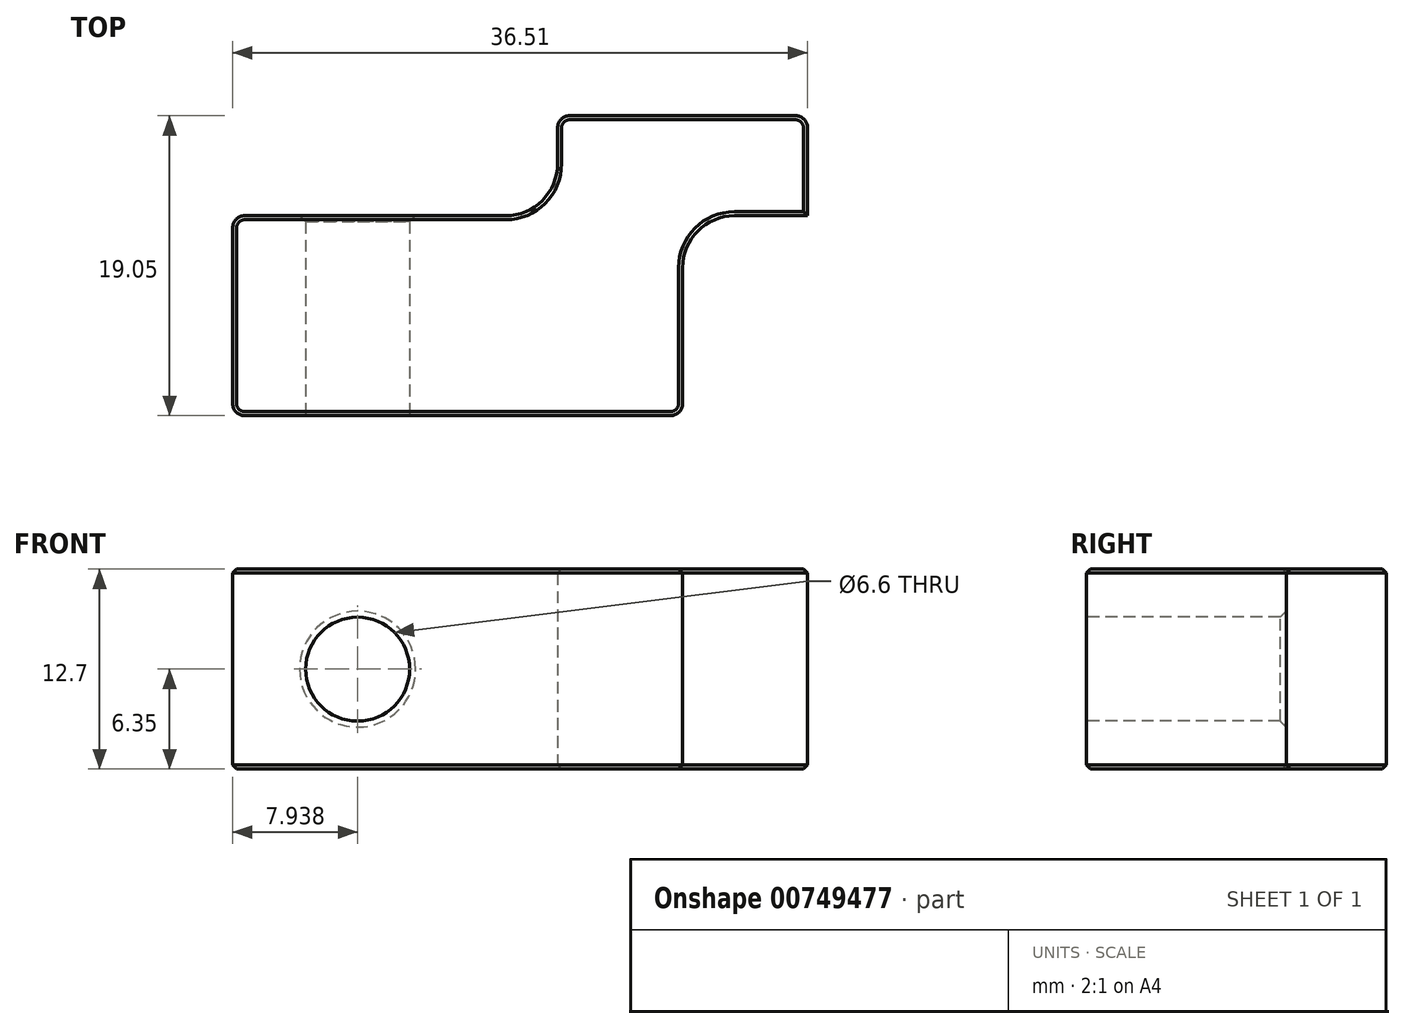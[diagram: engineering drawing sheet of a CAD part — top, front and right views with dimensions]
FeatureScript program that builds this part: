
annotation { "Feature Type Name" : "Feature", "Feature Type Description" : "" }
export const myFeature = defineFeature(function(context is Context, id is Id, definition is map)
    precondition{}
    {
        {
            var Q0;
            Q0=qCreatedBy(makeId("Top.planeOp"),FACE);
            var sketch = newSketch(context, id + "F0", { "sketchPlane" : qUnion([Q0])});
            skLineSegment(sketch, "E0", {"start": v(0, 0) * mm, "end": v(28.58, 0) * mm});
            skLineSegment(sketch, "E1", {"start": v(28.58, 0) * mm, "end": v(28.58, 9.4) * mm});
            skLineSegment(sketch, "E2", {"start": v(31.88, 12.7) * mm, "end": v(36.51, 12.7) * mm});
            skLineSegment(sketch, "E3", {"start": v(36.51, 12.7) * mm, "end": v(36.51, 19.05) * mm});
            skLineSegment(sketch, "E4", {"start": v(36.51, 19.05) * mm, "end": v(20.64, 19.05) * mm});
            skLineSegment(sketch, "E5", {"start": v(20.64, 19.05) * mm, "end": v(20.64, 16) * mm});
            skLineSegment(sketch, "E6", {"start": v(17.34, 12.7) * mm, "end": v(0, 12.7) * mm});
            skLineSegment(sketch, "E7", {"start": v(0, 12.7) * mm, "end": v(0, 0) * mm});
            skPoint(sketch, "E8.visualSharp", {"position": v(20.64, 12.7) * mm});
            skArc(sketch, "E8.filletArc", {"start": v(17.34, 12.7) * mm, "mid": v(19.67, 13.67) * mm, "end": v(20.64, 16) * mm});
            skPoint(sketch, "E9.visualSharp", {"position": v(28.58, 12.7) * mm});
            skArc(sketch, "E9.filletArc", {"start": v(31.88, 12.7) * mm, "mid": v(29.54, 11.73) * mm, "end": v(28.58, 9.4) * mm});
            skSolve(sketch);
        }
        {
            var Q0;
            Q0 = qSketchRegion(id + "F0", true);
            extrude(context, id + "F1", {"entities" : qUnion([Q0]), "depth" : 12.7 * mm, "offsetDistance" : 25.4 * mm});
        }
        {
            var Q0;
            Q0=makeQuery(id+"F1.opExtrude","SWEPT_EDGE",EDGE,{"disambiguationData":[OSD([sQuery(id+"F0.wireOp",EDGE,"E0"),sQuery(id+"F0.wireOp",EDGE,"E1")])]});
            var Q1;
            Q1=makeQuery(id+"F1.opExtrude","SWEPT_EDGE",EDGE,{"disambiguationData":[OSD([sQuery(id+"F0.wireOp",EDGE,"E0"),sQuery(id+"F0.wireOp",EDGE,"E7")])]});
            var Q2;
            Q2=makeQuery(id+"F1.opExtrude","SWEPT_EDGE",EDGE,{"disambiguationData":[OSD([sQuery(id+"F0.wireOp",EDGE,"E6"),sQuery(id+"F0.wireOp",EDGE,"E7")])]});
            var Q3;
            Q3=makeQuery(id+"F1.opExtrude","SWEPT_EDGE",EDGE,{"disambiguationData":[OSD([sQuery(id+"F0.wireOp",EDGE,"E4"),sQuery(id+"F0.wireOp",EDGE,"E5")])]});
            var Q4;
            Q4=makeQuery(id+"F1.opExtrude","SWEPT_EDGE",EDGE,{"disambiguationData":[OSD([sQuery(id+"F0.wireOp",EDGE,"E3"),sQuery(id+"F0.wireOp",EDGE,"E4")])]});
            fillet(context, id + "F2", {"entities" : qUnion([Q0, Q1, Q2, Q3, Q4]), "radius" : 0.76 * mm, "tangentPropagation" : true, "allowEdgeOverflow" : false});
        }
        {
            var Q0;
            Q0=makeQuery(id+"F1.opExtrude","SWEPT_FACE",FACE,{"disambiguationData":[OSD([sQuery(id+"F0.wireOp",EDGE,"E0")])]});
            var sketch = newSketch(context, id + "F3", { "sketchPlane" : qUnion([Q0])});
            skCircle(sketch, "E10", {"center": v(7.94, 6.35) * mm, "radius": 3.3 * mm});
            skSolve(sketch);
        }
        {
            var Q0;
            Q0 = qSketchRegion(id + "F3", true);
            extrude(context, id + "F4", {"entities" : qUnion([Q0]), "operationType" : NewBodyOperationType.REMOVE, "endBound" : BoundingType.THROUGH_ALL, "oppositeDirection" : true, "depth" : 25.4 * mm, "offsetDistance" : 25.4 * mm});
        }
        {
            var Q0;
            Q0=makeQuery(id+"F4.boolean.opBoolean","INTERSECT",EDGE,{"derivedFrom":[makeQuery(id+"F1.opExtrude","SWEPT_FACE",FACE,{"disambiguationData":[OSD([sQuery(id+"F0.wireOp",EDGE,"E6")])]}),makeQuery(id+"F4.opExtrude","SWEPT_FACE",FACE,{"disambiguationData":[OSD([sQuery(id+"F3.wireOp",EDGE,"E10")])]})]});
            var Q1;
            Q1=makeQuery(id+"F4.boolean.opBoolean","COPY",EDGE,{"derivedFrom":makeQuery(id+"F4.opExtrude","CAP_EDGE",EDGE,{"disambiguationData":[OSD([sQuery(id+"F3.wireOp",EDGE,"E10")])],"isStart":true})});
            chamfer(context, id + "F5", {"entities" : qUnion([Q0, Q1]), "width" : 0.38 * mm, "tangentPropagation" : true});
        }
        {
            var Q0;
            Q0=makeQuery(id+"F1.opExtrude","CAP_FACE",FACE,{"disambiguationData":[OSD([sQuery(id+"F0.wireOp",EDGE,"E0"),sQuery(id+"F0.wireOp",EDGE,"E1"),sQuery(id+"F0.wireOp",EDGE,"E2"),sQuery(id+"F0.wireOp",EDGE,"E3"),sQuery(id+"F0.wireOp",EDGE,"E4"),sQuery(id+"F0.wireOp",EDGE,"E5"),sQuery(id+"F0.wireOp",EDGE,"E6"),sQuery(id+"F0.wireOp",EDGE,"E7"),sQuery(id+"F0.wireOp",EDGE,"E8.filletArc"),sQuery(id+"F0.wireOp",EDGE,"E9.filletArc")])],"isStart":false});
            var Q1;
            Q1=makeQuery(id+"F1.opExtrude","CAP_FACE",FACE,{"disambiguationData":[OSD([sQuery(id+"F0.wireOp",EDGE,"E0"),sQuery(id+"F0.wireOp",EDGE,"E1"),sQuery(id+"F0.wireOp",EDGE,"E2"),sQuery(id+"F0.wireOp",EDGE,"E3"),sQuery(id+"F0.wireOp",EDGE,"E4"),sQuery(id+"F0.wireOp",EDGE,"E5"),sQuery(id+"F0.wireOp",EDGE,"E6"),sQuery(id+"F0.wireOp",EDGE,"E7"),sQuery(id+"F0.wireOp",EDGE,"E8.filletArc"),sQuery(id+"F0.wireOp",EDGE,"E9.filletArc")])],"isStart":true});
            chamfer(context, id + "F6", {"entities" : qUnion([Q0, Q1]), "width" : 0.25 * mm, "tangentPropagation" : true});
        }
    });
